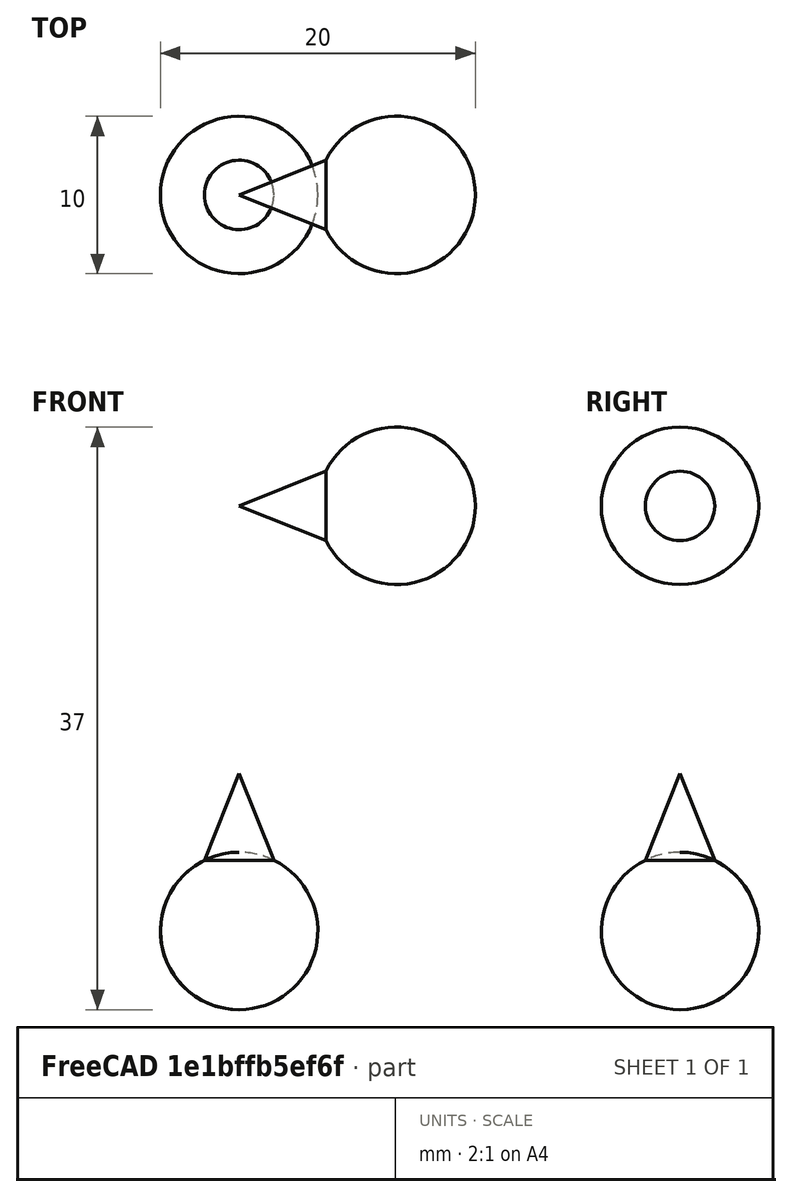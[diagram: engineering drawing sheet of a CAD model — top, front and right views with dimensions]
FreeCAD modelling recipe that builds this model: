
FCSTD DOCUMENT  (FreeCAD 0.22R35966 (Git))
Label: Bungee
License: All rights reserved
LicenseURL: http://en.wikipedia.org/wiki/All_rights_reserved
objects: App::DocumentObjectGroupPython×56, PartDesign::CoordinateSystem×10, App::Part×3, App::TextDocument×3, Part::Line×3, Part::Sphere×2, App::FeaturePython×2, Part::FeaturePython×2, Part::Cone×1, Part::MultiFuse×1, App::MaterialObjectPython×1, Points::Feature×1
note: 19 computed .brp shape members not serialized (recipe doc carries the construction recipe); baked Part::Feature solids carry a one-line shape summary decoded from their .brp

FEATURE [Part::Sphere] Sphere
  Angle1 = -90
  Angle2 = 90
  Angle3 = 360
  AttacherType = Attacher::AttachEngine3D
  Radius = 5
FEATURE [Part::Sphere] Sphere001
  Angle1 = -90
  Angle2 = 90
  Angle3 = 360
  AttacherType = Attacher::AttachEngine3D
  Radius = 5
FEATURE [App::Part] Part
  Group = -> [Sphere]
  Origin = -> Origin
FEATURE [Part::Cone] Cone
  Angle = 360
  AttacherType = Attacher::AttachEngine3D
  Height = 10
  Radius1 = 4
  Radius2 = 0
FEATURE [Part::MultiFuse] Fusion
  Shapes = -> [Sphere001,Cone]
FEATURE [App::Part] Part001
  Group = -> [Cone,Sphere001,Fusion]
  Origin = -> Origin001
  Placement = pos=(10,0,27) rot=(0,-1,0;1.5708rad)
FEATURE [App::DocumentObjectGroupPython] MBD_animated_vectors  # scripted group (container) (typed FeaturePython)
FEATURE [App::DocumentObjectGroupPython] MBD_constitutive_laws  # scripted group (container) (typed FeaturePython)
FEATURE [App::DocumentObjectGroupPython] MBD_drives_and_drive_callers  # scripted group (container) (typed FeaturePython)
FEATURE [App::DocumentObjectGroupPython] MBD_abstract_nodes  # scripted group (container) (typed FeaturePython)
FEATURE [App::DocumentObjectGroupPython] MBD_hydraulic_nodes  # scripted group (container) (typed FeaturePython)
FEATURE [App::DocumentObjectGroupPython] MBD_beam_elements  # scripted group (container) (typed FeaturePython)
FEATURE [App::DocumentObjectGroupPython] MBD_genel_clamps  # scripted group (container) (typed FeaturePython)
FEATURE [App::DocumentObjectGroupPython] MBD_genel_elements  # scripted group (container) (typed FeaturePython)
  Group = -> [MBD_genel_clamps]
FEATURE [App::DocumentObjectGroupPython] MBD_hydraulic_fluid_elements  # scripted group (container) (typed FeaturePython)
FEATURE [App::DocumentObjectGroupPython] MBD_hydraulic_elements  # scripted group (container) (typed FeaturePython)
  Group = -> [MBD_hydraulic_fluid_elements]
FEATURE [App::DocumentObjectGroupPython] MBD_angular_acceleration_joints  # scripted group (container) (typed FeaturePython)
FEATURE [App::DocumentObjectGroupPython] MBD_angular_velocity_joints  # scripted group (container) (typed FeaturePython)
FEATURE [App::DocumentObjectGroupPython] MBD_assembly_joints  # scripted group (container) (typed FeaturePython)
FEATURE [App::DocumentObjectGroupPython] MBD_coincidence_joints  # scripted group (container) (typed FeaturePython)
FEATURE [App::DocumentObjectGroupPython] MBD_cylindrical_joints  # scripted group (container) (typed FeaturePython)
FEATURE [App::DocumentObjectGroupPython] MBD_deformable_axial_joints  # scripted group (container) (typed FeaturePython)
FEATURE [App::DocumentObjectGroupPython] MBD_deformable_displacement_joints  # scripted group (container) (typed FeaturePython)
FEATURE [App::DocumentObjectGroupPython] MBD_deformable_hinge_joints  # scripted group (container) (typed FeaturePython)
FEATURE [App::DocumentObjectGroupPython] MBD_distance_joints  # scripted group (container) (typed FeaturePython)
FEATURE [App::DocumentObjectGroupPython] MBD_drive_hinge_joints  # scripted group (container) (typed FeaturePython)
FEATURE [App::DocumentObjectGroupPython] MBD_in_line_joints  # scripted group (container) (typed FeaturePython)
FEATURE [App::DocumentObjectGroupPython] MBD_in_plane_joints  # scripted group (container) (typed FeaturePython)
FEATURE [App::DocumentObjectGroupPython] MBD_linear_acceleration_joints  # scripted group (container) (typed FeaturePython)
FEATURE [App::DocumentObjectGroupPython] MBD_linear_velocity_joints  # scripted group (container) (typed FeaturePython)
FEATURE [App::DocumentObjectGroupPython] MBD_prismatic_joints  # scripted group (container) (typed FeaturePython)
FEATURE [App::DocumentObjectGroupPython] MBD_hinge_joints  # scripted group (container) (typed FeaturePython)
FEATURE [App::DocumentObjectGroupPython] MBD_revolute_pin_joints  # scripted group (container) (typed FeaturePython)
FEATURE [App::DocumentObjectGroupPython] MBD_revolute_rotation_joints  # scripted group (container) (typed FeaturePython)
FEATURE [App::DocumentObjectGroupPython] MBD_shock_absorber_joints  # scripted group (container) (typed FeaturePython)
FEATURE [App::DocumentObjectGroupPython] MBD_slider_joints  # scripted group (container) (typed FeaturePython)
FEATURE [App::DocumentObjectGroupPython] MBD_spherical_hinge_joints  # scripted group (container) (typed FeaturePython)
FEATURE [App::DocumentObjectGroupPython] MBD_total_joints  # scripted group (container) (typed FeaturePython)
FEATURE [App::DocumentObjectGroupPython] MBD_total_pin_joints  # scripted group (container) (typed FeaturePython)
FEATURE [App::DocumentObjectGroupPython] MBD_viscous_body_joints  # scripted group (container) (typed FeaturePython)
FEATURE [App::DocumentObjectGroupPython] MBD_dummy_body_elements  # scripted group (container) (typed FeaturePython)
FEATURE [App::DocumentObjectGroupPython] MBD_gear_body_elements  # scripted group (container) (typed FeaturePython)
FEATURE [App::DocumentObjectGroupPython] MBD_structural_couple_elements  # scripted group (container) (typed FeaturePython)
FEATURE [App::DocumentObjectGroupPython] MBD_scalar_functions  # scripted group (container) (typed FeaturePython)
FEATURE [App::TextDocument] ELEMENT_input_file
  Text = <blob: 10710 chars omitted>
FEATURE [App::TextDocument] ELEMENT_input_file_aux
FEATURE [App::DocumentObjectGroupPython] MBD_input_files  # scripted group (container) (typed FeaturePython)
  Group = -> [ELEMENT_input_file,ELEMENT_input_file_aux]
FEATURE [App::TextDocument] ELEMENT_variables
  Text = # For Z direction:\nK = 5; #Spring constant\nC = 0.02; #Damping constant\n\n# For x direction:\nK1 = 1; #Spring constant\nC1 = 0.01; #Damping constant
FEATURE [App::DocumentObjectGroupPython] MBD_user_defined_variables  # scripted group (container) (typed FeaturePython)
  Group = -> [ELEMENT_variables]
FEATURE [Part::Line] ELEMENT_cmx
  AttacherType = Attacher::AttachEngine3D
  X1 = -1e-16
  X2 = 0
  Y1 = -1e-16
  Y2 = 0
  Z1 = 2e-16
  Z2 = 27
FEATURE [Part::Line] ELEMENT_cmy
  AttacherType = Attacher::AttachEngine3D
  X1 = 0
  X2 = 0
  Y1 = 0
  Y2 = 0
  Z1 = 0
  Z2 = 1
FEATURE [Part::Line] ELEMENT_cmz
  AttacherType = Attacher::AttachEngine3D
  X1 = 0
  X2 = 0
  Y1 = 0
  Y2 = 0
  Z1 = 0
  Z2 = 1
FEATURE [PartDesign::CoordinateSystem] ELEMENT_ground
  AttacherType = Attacher::AttachEngine3D
FEATURE [App::DocumentObjectGroupPython] MBD_global_reference_frame  # scripted group (container) (typed FeaturePython)
  Group = -> [ELEMENT_cmx,ELEMENT_cmy,ELEMENT_cmz,ELEMENT_ground]
FEATURE [App::FeaturePython] ELEMENT_parameters  # WARN: FeaturePython — macro-defined, semantics opaque (R4)
  assembly_max_iterations = 1000
  default_orientation = 0
  derivatives_coefficient = auto
  derivatives_max_iterations = 100
  derivatives_tolerance = 0.0001
  final_time = 4
  initial_position_stiffness = 1
  initial_time = 0
  initial_velocity_stiffness = 1
  integration_max_iterations = 100
  model = 0
  modules_to_load = 0
  omega_rotates = 0
  output_data = 0
  output_meter = 1
  path_to_ELEMENT_executable = <userpath>/.local/share/FreeCAD/Mod/FreeCAD-motion-workbench-master/mbdyn-1.7.3-executables/LinuxExecutable/mbdyn
  print = 0
  skip_initial_joint_assembly = 0
  solver = 0
  time_step = 0.01
  tolerance = 1e-06
  type_of_path_to_ELEMENT_executable = 0
  type_of_path_to_run_time_loadable_modules = 0
  type_of_working_directory = 0
  units = 0
FEATURE [App::FeaturePython] ELEMENT_animation  # WARN: FeaturePython — macro-defined, semantics opaque (R4)
  animationClicked = false
  assembled = false
  association0 = none
  association1 = none
  association2 = none
  association3 = none
  association4 = none
  association5 = none
  association6 = none
  association7 = none
  association8 = none
  association9 = none
  bodies_line_width = 1
  bodies_point_size = 4
  characteristic_length = 47.9751
  continous = true
  current_time = 0
  current_time_step = 0
  follow_selected_object = false
  highlight_element = true
  objects_to_animate = 0
  speed = 10
  stop_at_time = 0
  stop_at_time_step = 0
  subAssembly = true
  transparency_when_assembled = 0
  transparency_when_exploded = 50
  zoon_when_contracted = 0.5
  zoon_when_expanded = 1
FEATURE [App::DocumentObjectGroupPython] MBD_simulation_parameters  # scripted group (container) (typed FeaturePython)
  Group = -> [ELEMENT_parameters,ELEMENT_animation]
FEATURE [Part::FeaturePython] ELEMENT_static_body_1  # WARN: FeaturePython — macro-defined, semantics opaque (R4)
  absolute_center_of_mass_X = 0
  absolute_center_of_mass_Y = -1e-16
  absolute_center_of_mass_Z = -1e-16
  base_entity = Part
  label = 1
  type = static
FEATURE [App::DocumentObjectGroupPython] MBD_static_body_elements  # scripted group (container) (typed FeaturePython)
  Group = -> [ELEMENT_static_body_1]
FEATURE [PartDesign::CoordinateSystem] ELEMENT_structural_static_1
  AttacherType = Attacher::AttachEngine3D
  Placement = pos=(0,-1e-16,-1e-16) rot=(0,0,1;0rad)
  absolute_angular_velocity_X = 0
  absolute_angular_velocity_Y = 0
  absolute_angular_velocity_Z = 0
  absolute_orientation_matrix = 3, 0.0, 0.0, 1.0, 2, 0.0, 1.0, 0.0
  absolute_position_X = 0
  absolute_position_Y = -1e-16
  absolute_position_Z = -1e-16
  absolute_velocity_X = 0
  absolute_velocity_Y = 0
  absolute_velocity_Z = 0
  base_entity = -> ELEMENT_static_body_1
  initial_conditions_reference_system_angular_velocity = 0
  initial_conditions_reference_system_velocity = 0
  label = 1
  offset_pitch = 0
  offset_reference_system_orientation = 0
  offset_reference_system_position = 0
  offset_roll = 0
  offset_x = 0
  offset_y = 0
  offset_yaw = 0
  offset_z = 0
  placement_method = 0
  plugin_variables = none
  type = static
FEATURE [App::DocumentObjectGroupPython] MBD_structural_static_nodes  # scripted group (container) (typed FeaturePython)
  Group = -> [ELEMENT_structural_static_1]
FEATURE [PartDesign::CoordinateSystem] ELEMENT_clamp_joint_1
  AttacherType = Attacher::AttachEngine3D
  Placement = pos=(0,-1e-16,-1e-16) rot=(0,0,1;0rad)
  absolute_orientation_matrix = 3, 0.0, 0.0, 1.0, 2, 0.0, 1.0, 0.0
  absolute_pin_position_X = 0
  absolute_pin_position_Y = -1e-16
  absolute_pin_position_Z = -1e-16
  assembly_joint = true
  base_entity = -> ELEMENT_static_body_1
  driven_element = false
  driven_element_expression = Time <= 1.0
  group = 0
  joint = clamp
  joint_activation = 0
  label = 1
  plugin_variables = none
FEATURE [App::DocumentObjectGroupPython] MBD_clamp_joints  # scripted group (container) (typed FeaturePython)
  Group = -> [ELEMENT_clamp_joint_1]
FEATURE [App::DocumentObjectGroupPython] MBD_joint_elements  # scripted group (container) (typed FeaturePython)
  Group = -> [MBD_angular_acceleration_joints,MBD_angular_velocity_joints,MBD_assembly_joints,MBD_clamp_joints,MBD_coincidence_joints,MBD_cylindrical_joints,MBD_deformable_axial_joints,MBD_deformable_displacement_joints,MBD_deformable_hinge_joints,MBD_distance_joints,MBD_drive_hinge_joints,MBD_in_line_joints,MBD_in_plane_joints,MBD_linear_acceleration_joints,MBD_linear_velocity_joints,MBD_prismatic_joints,+9 more]
FEATURE [PartDesign::CoordinateSystem] ELEMENT_gravity_1
  AttacherType = Attacher::AttachEngine3D
  direction = 0.0, 0.0, 1.0
  driven_element = false
  driven_element_expression = Time < 4.
  gravity_acceleration = 9.807
  label = 1
  offset_pitch = 0
  offset_reference_system_orientation = 0
  offset_reference_system_position = 0
  offset_roll = 0
  offset_x = 0
  offset_y = 0
  offset_yaw = 0
  offset_z = 0
  placement_method = 1
  type = uniform
FEATURE [App::DocumentObjectGroupPython] MBD_gravity_elements  # scripted group (container) (typed FeaturePython)
  Group = -> [ELEMENT_gravity_1]
FEATURE [Part::FeaturePython] ELEMENT_rigid_body_2  # WARN: FeaturePython — macro-defined, semantics opaque (R4)
  FirstAxisOfInertia = (0.96,0.27,0)
  Ixx = 0.0483899
  Iyy = 0.0483899
  Izz = 0.0416362
  Placement = pos=(10,0,27) rot=(0,-1,0;1.5708rad)
  SecondAxisOfInertia = (-0.27,0.96,0)
  ThirdAxisOfInertia = (0,0,1)
  absolute_center_of_mass_X = 9.73331
  absolute_center_of_mass_Y = 1e-16
  absolute_center_of_mass_Z = 27
  base_entity = Part001
  density = 7.9e-06
  ixx = 6125.3
  iyy = 6125.3
  izz = 5270.41
  label = 2
  mass = 0.00432668
  material = Steel-Generic
  material_definition = 0
  material_object = ELEMENT_material_2
  node = 2
  relative_center_of_mass_X = 0
  relative_center_of_mass_Y = 0
  relative_center_of_mass_Z = 0
  type = rigid
  volume = 547.681
FEATURE [App::DocumentObjectGroupPython] MBD_rigid_body_elements  # scripted group (container) (typed FeaturePython)
  Group = -> [ELEMENT_rigid_body_2]
FEATURE [App::Part] MBD_body_elements
  Group = -> [MBD_dummy_body_elements,MBD_rigid_body_elements,MBD_gear_body_elements,MBD_static_body_elements,ELEMENT_static_body_1,ELEMENT_rigid_body_2]
  Origin = -> Origin002
FEATURE [App::MaterialObjectPython] ELEMENT_material_2  # material (typed FeaturePython)
  Category = 0
  Material = Density=7900.00 kg/m^3; Name=Steel-Generic
FEATURE [App::DocumentObjectGroupPython] MBD_materials  # scripted group (container) (typed FeaturePython)
  Group = -> [ELEMENT_material_2]
FEATURE [PartDesign::CoordinateSystem] ELEMENT_structural_dynamic_2
  AttacherType = Attacher::AttachEngine3D
  Placement = pos=(9.73331,1e-16,27) rot=(0,-1,0;1.5708rad)
  absolute_angular_velocity_X = 0
  absolute_angular_velocity_Y = 0
  absolute_angular_velocity_Z = 0
  absolute_orientation_matrix = 3, -1.0, -0.0, 2.220446049250313e-16, 2, -0.0, 1.0, 0.0
  absolute_position_X = 9.73331
  absolute_position_Y = 1e-16
  absolute_position_Z = 27
  absolute_velocity_X = 0
  absolute_velocity_Y = 0
  absolute_velocity_Z = 0
  base_entity = -> ELEMENT_rigid_body_2
  initial_conditions_reference_system_angular_velocity = 0
  initial_conditions_reference_system_velocity = 0
  label = 2
  offset_pitch = 0
  offset_reference_system_orientation = 0
  offset_reference_system_position = 0
  offset_roll = 0
  offset_x = 0
  offset_y = 0
  offset_yaw = 0
  offset_z = 0
  placement_method = 0
  plugin_variables = none
  type = dynamic
FEATURE [App::DocumentObjectGroupPython] MBD_structural_dynamic_nodes  # scripted group (container) (typed FeaturePython)
  Group = -> [ELEMENT_structural_dynamic_2]
FEATURE [PartDesign::CoordinateSystem] ELEMENT_structural_dummy_3
  AttacherType = Attacher::AttachEngine3D
  Placement = pos=(0,0,27) rot=(0,0,1;0rad)
  absolute_position_X = 0
  absolute_position_Y = 0
  absolute_position_Z = 27
  base_entity = -> ELEMENT_rigid_body_2
  dummy_node_type = 0
  label = 3
  offset_pitch = 0
  offset_reference_system_orientation = 0
  offset_reference_system_position = 0
  offset_roll = 0
  offset_x = 0
  offset_y = 0
  offset_yaw = 0
  offset_z = 0
  placement_method = 1
  plugin_variables = "X_1_3": position in global direction 1 \n"X_3_3": position in global direction 3 \n"XP_1_3": velocity in global direction 1 \n"XP_3_3": velocity in global direction 3
  position_reference_1 = -> ELEMENT_rigid_body_2 [Vertex3]
  relative_offset_X = 0
  relative_offset_Y = -1e-16
  relative_offset_Z = 9.73331
  relative_orientation_matrix = 3, 1.0, 0.0, 2.220446049250313e-16, 2, 0.0, 1.0, 0.0
  type = dummy
FEATURE [App::DocumentObjectGroupPython] MBD_structural_dummy_nodes  # scripted group (container) (typed FeaturePython)
  Group = -> [ELEMENT_structural_dummy_3]
FEATURE [App::DocumentObjectGroupPython] MBD_nodes  # scripted group (container) (typed FeaturePython)
  Group = -> [MBD_abstract_nodes,MBD_structural_dummy_nodes,MBD_structural_dynamic_nodes,MBD_hydraulic_nodes,MBD_structural_static_nodes]
FEATURE [PartDesign::CoordinateSystem] ELEMENT_marker_2_1
  AttacherType = Attacher::AttachEngine3D
  Placement = pos=(0,0,27) rot=(1,0,0;3.14159rad)
  base_entity = -> ELEMENT_rigid_body_2
  label = 2
  offset_pitch = 0
  offset_reference_system_orientation = 0
  offset_reference_system_position = 0
  offset_roll = 0
  offset_x = 0
  offset_y = 0
  offset_yaw = 0
  offset_z = 0
  placement_method = 1
  position_reference_1 = -> ELEMENT_rigid_body_2 [Vertex3]
FEATURE [PartDesign::CoordinateSystem] ELEMENT_structural_internal_force_1
  AttacherType = Attacher::AttachEngine3D
  Placement = pos=(-1e-16,-1e-16,2e-16) rot=(0,0,1;0rad)
  action_entity = -> ELEMENT_marker_2_1
  base_entity = -> ELEMENT_static_body_1
  contact_damping_activation_depth = 1e-06
  contact_damping_coefficient = 10
  contact_direction = 0
  contact_model = 0
  contact_offset = 0
  contact_stiffness_coefficient = 1000000
  contact_stiffness_exponent = 1.2
  contact_type = 0
  direction = 0.0, 0.0, 1.0
  driven_element_expression = Time <= 1.0
  element_activation = 0
  force = structural internal force
  force_value = K * (X_3_3 - Pz_2) + C * XP_3_3
  label = 1
  offset_pitch = 0
  offset_reference_system_orientation = 0
  offset_reference_system_position = 0
  offset_roll = 0
  offset_x = 0
  offset_y = 0
  offset_yaw = 0
  offset_z = 0
  placement_method = 1
  position_reference_1 = -> ELEMENT_static_body_1 [Face1]
  relative_arm_1 = -8.794367491272882e-20, -8.188652633034113e-20, 2.4513724383723465e-19
  relative_arm_2 = 0.0, -1.1435427334499558e-19, 0.009733309626805896
  type = 1
FEATURE [PartDesign::CoordinateSystem] ELEMENT_marker_2_2
  AttacherType = Attacher::AttachEngine3D
  Placement = pos=(0,0,27) rot=(0.707107,0,-0.707107;3.14159rad)
  base_entity = -> ELEMENT_rigid_body_2
  label = 2
  offset_pitch = 0
  offset_reference_system_orientation = 0
  offset_reference_system_position = 0
  offset_roll = 0
  offset_x = 0
  offset_y = 0
  offset_yaw = 0
  offset_z = 0
  placement_method = 1
  position_reference_1 = -> ELEMENT_rigid_body_2 [Vertex3]
FEATURE [App::DocumentObjectGroupPython] MBD_markers  # scripted group (container) (typed FeaturePython)
  Group = -> [ELEMENT_marker_2_1,ELEMENT_marker_2_2]
FEATURE [PartDesign::CoordinateSystem] ELEMENT_structural_internal_force_2
  AttacherType = Attacher::AttachEngine3D
  Placement = pos=(-1e-16,-1e-16,2e-16) rot=(0,1,0;1.5708rad)
  action_entity = -> ELEMENT_marker_2_2
  base_entity = -> ELEMENT_static_body_1
  contact_damping_activation_depth = 1e-06
  contact_damping_coefficient = 10
  contact_direction = 0
  contact_model = 0
  contact_offset = 0
  contact_stiffness_coefficient = 1000000
  contact_stiffness_exponent = 1.2
  contact_type = 0
  direction = 1.0, 0.0, 2.220446049250313e-16
  driven_element_expression = Time <= 1.0
  element_activation = 0
  force = structural internal force
  force_value = K1* (X_1_3 - Px_2) + C1 * XP_1_3 + 0.01
  label = 2
  offset_pitch = 90
  offset_reference_system_orientation = 0
  offset_reference_system_position = 0
  offset_roll = 0
  offset_x = 0
  offset_y = 0
  offset_yaw = 0
  offset_z = 0
  placement_method = 1
  position_reference_1 = -> ELEMENT_static_body_1 [Face1]
  relative_arm_1 = -8.794367491272882e-20, -8.188652633034113e-20, 2.4513724383723465e-19
  relative_arm_2 = 0.0, -1.1435427334499558e-19, 0.009733309626805896
  type = 1
FEATURE [App::DocumentObjectGroupPython] MBD_structural_force_elements  # scripted group (container) (typed FeaturePython)
  Group = -> [ELEMENT_structural_internal_force_1,ELEMENT_structural_internal_force_2]
FEATURE [App::DocumentObjectGroupPython] MBD_elements  # scripted group (container) (typed FeaturePython)
  Group = -> [MBD_beam_elements,MBD_body_elements,MBD_genel_elements,MBD_gravity_elements,MBD_hydraulic_elements,MBD_joint_elements,MBD_structural_couple_elements,MBD_structural_force_elements]
FEATURE [App::DocumentObjectGroupPython] MBD_simulation  # scripted group (container) (typed FeaturePython)
  Group = -> [MBD_animated_vectors,MBD_constitutive_laws,MBD_drives_and_drive_callers,MBD_global_reference_frame,MBD_input_files,MBD_materials,MBD_markers,MBD_nodes,MBD_elements,MBD_simulation_parameters,MBD_scalar_functions,MBD_user_defined_variables]
FEATURE [Points::Feature] cloud
